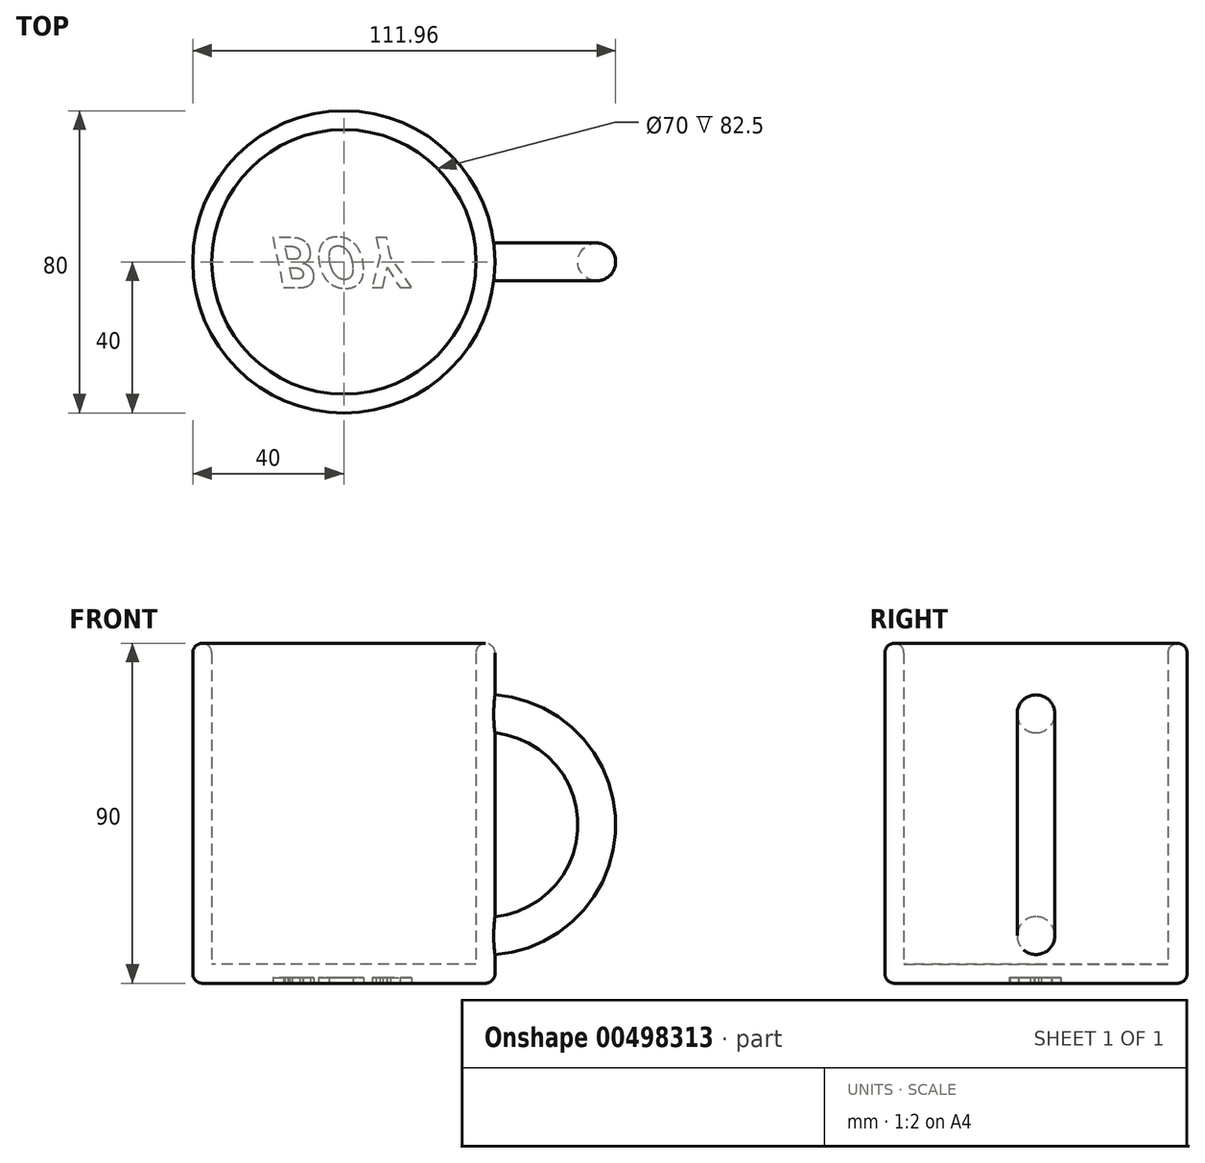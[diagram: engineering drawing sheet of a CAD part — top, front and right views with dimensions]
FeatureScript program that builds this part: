
annotation { "Feature Type Name" : "Feature", "Feature Type Description" : "" }
export const myFeature = defineFeature(function(context is Context, id is Id, definition is map)
    precondition{}
    {
        {
            var Q0;
            Q0=qCreatedBy(makeId("Top.planeOp"),FACE);
            var sketch = newSketch(context, id + "F0", { "sketchPlane" : qUnion([Q0])});
            skCircle(sketch, "E0", {"center": v(0, 0) * mm, "radius": 40 * mm});
            skSolve(sketch);
        }
        {
            var Q0;
            Q0=makeQuery(id+"F0.imprint","IMPRINT",FACE,{"disambiguationData":[TD([[makeQuery(id+"F0.imprint","IMPRINT",EDGE,{"derivedFrom":sQuery(id+"F0.wireOp",EDGE,"E0")}),1.0]])]});
            extrude(context, id + "F1", {"entities" : qUnion([Q0]), "depth" : 90 * mm});
        }
        {
            var Q0;
            Q0=makeQuery(id+"F1.opExtrude","CAP_FACE",FACE,{"disambiguationData":[OSD([sQuery(id+"F0.wireOp",EDGE,"E0")])],"isStart":false});
            shell(context, id + "F2", {"entities" : qUnion([Q0]), "thickness" : 5 * mm});
        }
        {
            var Q0;
            Q0=qCreatedBy(makeId("Right.planeOp"),FACE);
            cPlane(context, id + "F3", {"entities" : qUnion([Q0]), "cplaneType" : CPlaneType.OFFSET, "offset" : 37.5 * mm, "width" : 150 * mm, "height" : 150 * mm});
        }
        {
            var Q0;
            Q0=qCreatedBy(id+"F3.planeOp",FACE);
            var sketch = newSketch(context, id + "F4", { "sketchPlane" : qUnion([Q0])});
            skCircle(sketch, "E1", {"center": v(0, 71.44) * mm, "radius": 5 * mm});
            skLineSegment(sketch, "E2", {"start": v(0, 41.97) * mm, "end": v(25.63, 41.97) * mm});
            skSolve(sketch);
        }
        {
            var Q0;
            Q0 = qSketchRegion(id + "F4", true);
            var Q1;
            Q1=sQuery(id+"F4.wireOp",EDGE,"E2");
            revolve(context, id + "F5", {"operationType" : NewBodyOperationType.ADD, "entities" : qUnion([Q0]), "axis" : qUnion([Q1]), "revolveType" : RevolveType.ONE_DIRECTION, "angle" : 180 * degree});
        }
        {
            var Q0;
            Q0=makeQuery(id+"F1.opExtrude","CAP_EDGE",EDGE,{"disambiguationData":[OSD([sQuery(id+"F0.wireOp",EDGE,"E0")])],"isStart":false});
            var Q1;
            {var subQ0=sQuery(id+"F0.wireOp",EDGE,"E0");Q1=makeQuery(id+"F2.opShell","OFFSET_EDGE",EDGE,{"disambiguationData":[OSD([subQ0]),TDD([makeQuery(id+"F1.opExtrude","CAP_EDGE",EDGE,{"disambiguationData":[OSD([subQ0])],"isStart":false})])]});}
            var Q2;
            Q2=makeQuery(id+"F1.opExtrude","CAP_EDGE",EDGE,{"disambiguationData":[OSD([sQuery(id+"F0.wireOp",EDGE,"E0")])],"isStart":true});
            fillet(context, id + "F6", {"entities" : qUnion([Q0, Q1, Q2]), "radius" : 2.5 * mm, "tangentPropagation" : true, "allowEdgeOverflow" : false});
        }
        {
            var Q0;
            Q0=makeQuery(id+"F1.opExtrude","CAP_FACE",FACE,{"disambiguationData":[OSD([sQuery(id+"F0.wireOp",EDGE,"E0")])],"isStart":true});
            var sketch = newSketch(context, id + "F7", { "sketchPlane" : qUnion([Q0])});
            skText(sketch, "E3", { "text": "BOY", "fontName": "OpenSans-BoldItalic.ttf"});
            const initialGuessF7  = {"E3": [-0.0193, -0.00644, 1, 0, 0.01338]};
            skSetInitialGuess(sketch, initialGuessF7);
            skSolve(sketch);
        }
        {
            var Q0;
            Q0 = qSketchRegion(id + "F7", true);
            extrude(context, id + "F8", {"entities" : qUnion([Q0]), "operationType" : NewBodyOperationType.REMOVE, "oppositeDirection" : true, "depth" : 1.5 * mm});
        }
    });
